# Revit family: AFX-Cass-Led_Pendant-1
name_source: partatom
category: Lighting Fixtures
units: mm (PartAtom-declared; Revit-internal decimal feet)

## family parameters
Cut with Voids When Loaded = No
Host = Face
Light Source = Yes
Part Type = Normal
Room Calculation Point = No
Round Connector Dimension = Use Diameter
Shared = No

## types (4) — shared parameters
Apparent Load = 0 VA
Assembly Code = D5020200
Canopy Finish = AFX - Aluminum Black
Color Filter = 16777215
Colour Rendering Index = 90
Cord Finish = AFX - Plastic Black
Default Elevation = 48"
Diameter = 4"
Diffuser Finish = AFX - White Acrylic
Dimming Lamp Color Temperature Shift = <None>
Emit Shape Visible in Rendering = No
Emit from Circle Diameter = 24"
Frame Finish = AFX - Aluminum Black
Keynote = 12500
Manufacturer = AFX Inc
Product Documentation Link = https://www.afxinc.com
Support Finish = AFX - Aluminum Black
Tilt Angle = -90.00°
Type Comments = Cass
URL = https://www.afxinc.com
Voltage = 120 V

## per-type parameters (varying)
| type | Description | Dist Ies | Distance Body | Height | Photometric Web File | Wattage Comments |
| CSSP12L30D1BK | Contemporary LED linear pendant with four sided illumination White acrylic diffuser and 9 ft adjustable cord - 4"Diameter x 12"H | 0" | 6" | 12" | CSSP12L30D1XX.IES | 15W |
| CSSP24L30D1BK | Contemporary LED linear pendant with four sided illumination White acrylic diffuser and 9 ft adjustable cord - 4"Diameter x 24"H | 10" | 12" | 24" | CSSP24L30D1XX.IES | 25W |
| CSSP36L30D1BK | Contemporary LED linear pendant with four sided illumination White acrylic diffuser and 9 ft adjustable cord - 4"Diameter x 36"H | 18" | 18" | 36" | CSSP36L30D1XX.IES | 36W |
| CSSP48L30D1BK | Contemporary LED linear pendant with four sided illumination White acrylic diffuser and 9 ft adjustable cord - 4"Diameter x 48"H | 24" | 24" | 48" | CSSP48L30D1XX.IES | 40W |

note: column(s) folded — value = type name in every type: Model

## geometry (parser evidence)
native form markers: Sweep x4
no freeform markers — native parametric forms only
